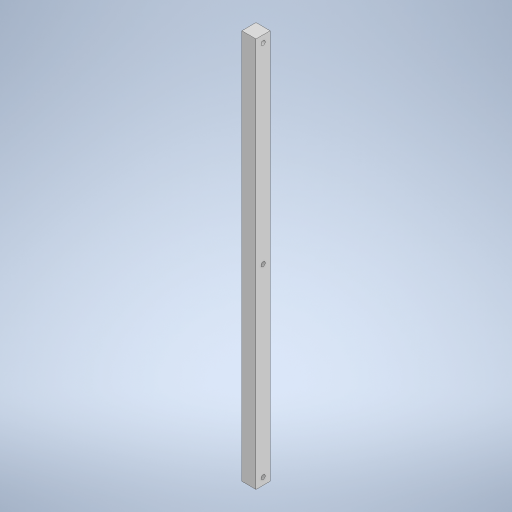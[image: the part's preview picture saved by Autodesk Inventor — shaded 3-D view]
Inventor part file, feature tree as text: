
AUTODESK INVENTOR PART (.ipt)
format: ipt  version: 2023 (Build 270158000, 158)  size: 245,248 bytes
history: native  units: mm
features: sketch x2, other x1, extrude x1, hole x1
ambient origin geometry x8: Origin, YZ Plane, XZ Plane, XY Plane, X Axis, Y Axis, Z Axis, Center Point
bodies: Body1 (feature_tree)
feature tree (5):
  other  "ソリッド1"
  extrude  "押し出し1"  Depth=10.0mm
  hole  "穴1"  [1 undecoded]
  sketch  "スケッチ1"
  sketch  "スケッチ2"
note: 1 required parameter value undecoded (feature->parameter linkage not recoverable at this tier; creation-order binding heuristic only, values carry confidence <= 0.55)
